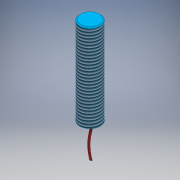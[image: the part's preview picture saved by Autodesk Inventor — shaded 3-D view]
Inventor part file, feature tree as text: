
AUTODESK INVENTOR PART (.ipt)
format: ipt  version: 2018 (Build 220112000, 112)  size: 144,384 bytes
history: native  units: mm
features: sketch x3, extrude x1, thread x1, chamfer x1, sweep x1
ambient origin geometry x8: Origin, YZ Plane, XZ Plane, XY Plane, X Axis, Y Axis, Z Axis, Center Point
bodies: Solido1 (feature_tree)
feature tree (7):
  extrude  "Estrusione1"  Depth=18.0mm
  thread  "Filettatura1"
  chamfer  "Smusso1"  Distance=77.0mm
  sweep  "Sweep1"
  sketch  "Schizzo1"
  sketch  "Schizzo3"
  sketch  "Schizzo4"
